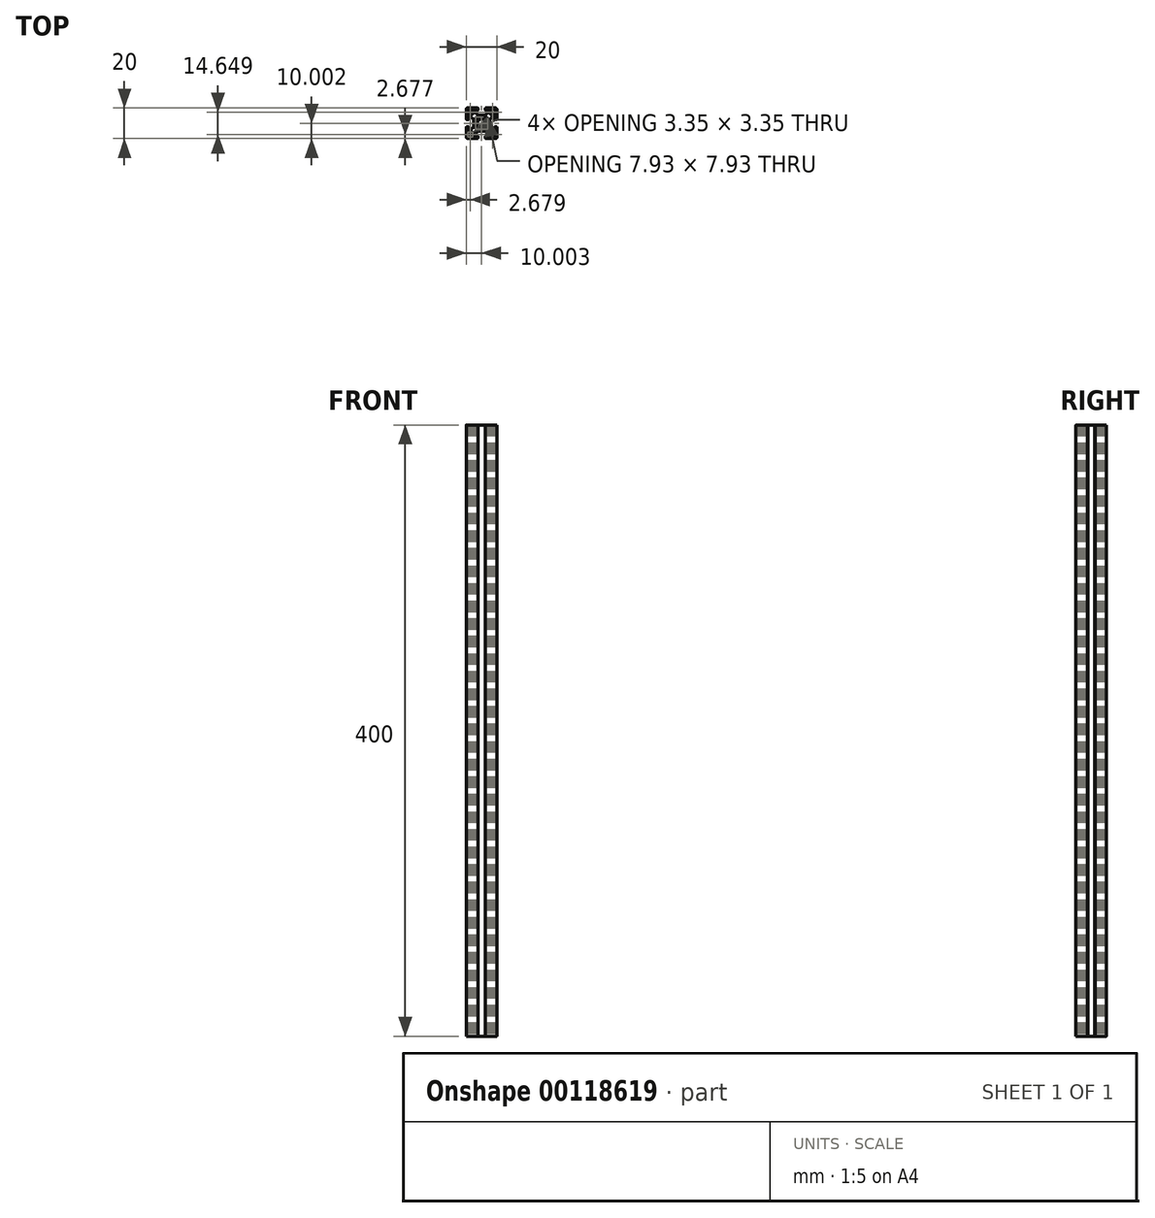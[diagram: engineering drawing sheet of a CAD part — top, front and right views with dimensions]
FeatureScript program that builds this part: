
annotation { "Feature Type Name" : "Feature", "Feature Type Description" : "" }
export const myFeature = defineFeature(function(context is Context, id is Id, definition is map)
    precondition{}
    {
        {
            var Q0;
            Q0=qCreatedBy(makeId("Top.planeOp"),FACE);
            var sketch = newSketch(context, id + "F0", { "sketchPlane" : qUnion([Q0])});
            skLineSegment(sketch, "E0", {"start": v(121.03, 63.35) * mm, "end": v(114.47, 63.35) * mm});
            skLineSegment(sketch, "E1", {"start": v(121.03, 43.35) * mm, "end": v(114.47, 43.35) * mm});
            skLineSegment(sketch, "E2", {"start": v(121.83, 62.55) * mm, "end": v(121.83, 56) * mm});
            skLineSegment(sketch, "E3", {"start": v(101.83, 62.55) * mm, "end": v(101.83, 56) * mm});
            skLineSegment(sketch, "E4", {"start": v(114.18, 58.55) * mm, "end": v(109.48, 58.55) * mm});
            skArc(sketch, "E5", {"start": v(114.47, 63.35) * mm, "mid": v(114.3, 63.28) * mm, "end": v(114.23, 63.11) * mm});
            skLineSegment(sketch, "E6", {"start": v(116.63, 61.75) * mm, "end": v(114.47, 61.75) * mm});
            skArc(sketch, "E7", {"start": v(114.23, 62) * mm, "mid": v(114.3, 61.82) * mm, "end": v(114.47, 61.75) * mm});
            skLineSegment(sketch, "E8", {"start": v(109.2, 61.75) * mm, "end": v(107.03, 61.75) * mm});
            skArc(sketch, "E9", {"start": v(109.2, 61.75) * mm, "mid": v(109.36, 61.82) * mm, "end": v(109.43, 62) * mm});
            skLineSegment(sketch, "E10", {"start": v(107.03, 61) * mm, "end": v(107.03, 61.75) * mm});
            skLineSegment(sketch, "E11", {"start": v(116.63, 61) * mm, "end": v(116.63, 61.75) * mm});
            skLineSegment(sketch, "E12", {"start": v(109.43, 62) * mm, "end": v(109.43, 63.11) * mm});
            skArc(sketch, "E13", {"start": v(109.43, 63.11) * mm, "mid": v(109.36, 63.28) * mm, "end": v(109.2, 63.35) * mm});
            skLineSegment(sketch, "E14", {"start": v(114.23, 62) * mm, "end": v(114.23, 63.11) * mm});
            skLineSegment(sketch, "E15", {"start": v(109.48, 58.55) * mm, "end": v(107.03, 61) * mm});
            skLineSegment(sketch, "E16", {"start": v(114.18, 58.55) * mm, "end": v(116.63, 61) * mm});
            skLineSegment(sketch, "E17", {"start": v(114.18, 48.15) * mm, "end": v(109.48, 48.15) * mm});
            skArc(sketch, "E18", {"start": v(114.23, 43.6) * mm, "mid": v(114.3, 43.42) * mm, "end": v(114.47, 43.35) * mm});
            skLineSegment(sketch, "E19", {"start": v(116.63, 44.95) * mm, "end": v(114.47, 44.95) * mm});
            skArc(sketch, "E20", {"start": v(114.47, 44.95) * mm, "mid": v(114.3, 44.88) * mm, "end": v(114.23, 44.71) * mm});
            skLineSegment(sketch, "E21", {"start": v(109.2, 44.95) * mm, "end": v(107.03, 44.95) * mm});
            skArc(sketch, "E22", {"start": v(109.43, 44.71) * mm, "mid": v(109.36, 44.88) * mm, "end": v(109.2, 44.95) * mm});
            skLineSegment(sketch, "E23", {"start": v(107.03, 45.7) * mm, "end": v(107.03, 44.95) * mm});
            skLineSegment(sketch, "E24", {"start": v(116.63, 45.7) * mm, "end": v(116.63, 44.95) * mm});
            skLineSegment(sketch, "E25", {"start": v(109.43, 44.71) * mm, "end": v(109.43, 43.6) * mm});
            skArc(sketch, "E26", {"start": v(109.2, 43.35) * mm, "mid": v(109.36, 43.42) * mm, "end": v(109.43, 43.6) * mm});
            skLineSegment(sketch, "E27", {"start": v(114.23, 44.71) * mm, "end": v(114.23, 43.6) * mm});
            skLineSegment(sketch, "E28", {"start": v(109.48, 48.15) * mm, "end": v(107.03, 45.7) * mm});
            skLineSegment(sketch, "E29", {"start": v(114.18, 48.15) * mm, "end": v(116.63, 45.7) * mm});
            skLineSegment(sketch, "E30", {"start": v(117.03, 51) * mm, "end": v(117.03, 55.7) * mm});
            skArc(sketch, "E31", {"start": v(121.83, 50.71) * mm, "mid": v(121.76, 50.88) * mm, "end": v(121.6, 50.95) * mm});
            skLineSegment(sketch, "E32", {"start": v(120.23, 48.55) * mm, "end": v(120.23, 50.71) * mm});
            skArc(sketch, "E33", {"start": v(120.47, 50.95) * mm, "mid": v(120.3, 50.88) * mm, "end": v(120.23, 50.71) * mm});
            skLineSegment(sketch, "E34", {"start": v(120.23, 56) * mm, "end": v(120.23, 58.15) * mm});
            skArc(sketch, "E35", {"start": v(120.23, 56) * mm, "mid": v(120.3, 55.82) * mm, "end": v(120.47, 55.75) * mm});
            skLineSegment(sketch, "E36", {"start": v(119.48, 58.15) * mm, "end": v(120.23, 58.15) * mm});
            skLineSegment(sketch, "E37", {"start": v(119.48, 48.55) * mm, "end": v(120.23, 48.55) * mm});
            skLineSegment(sketch, "E38", {"start": v(120.47, 55.75) * mm, "end": v(121.6, 55.75) * mm});
            skArc(sketch, "E39", {"start": v(121.6, 55.75) * mm, "mid": v(121.76, 55.82) * mm, "end": v(121.83, 56) * mm});
            skLineSegment(sketch, "E40", {"start": v(120.47, 50.95) * mm, "end": v(121.6, 50.95) * mm});
            skLineSegment(sketch, "E41", {"start": v(117.03, 55.7) * mm, "end": v(119.48, 58.15) * mm});
            skLineSegment(sketch, "E42", {"start": v(117.03, 51) * mm, "end": v(119.48, 48.55) * mm});
            skArc(sketch, "E43", {"start": v(113.06, 55.78) * mm, "mid": v(111.83, 56.07) * mm, "end": v(110.6, 55.78) * mm});
            skArc(sketch, "E44", {"start": v(109.4, 54.58) * mm, "mid": v(109.11, 53.35) * mm, "end": v(109.4, 52.12) * mm});
            skArc(sketch, "E45", {"start": v(110.6, 50.93) * mm, "mid": v(111.83, 50.63) * mm, "end": v(113.06, 50.93) * mm});
            skArc(sketch, "E46", {"start": v(113.34, 50.88) * mm, "mid": v(113.2, 50.95) * mm, "end": v(113.06, 50.93) * mm});
            skArc(sketch, "E47", {"start": v(113.06, 55.78) * mm, "mid": v(113.2, 55.75) * mm, "end": v(113.34, 55.82) * mm});
            skArc(sketch, "E48", {"start": v(114.26, 52.12) * mm, "mid": v(114.55, 53.35) * mm, "end": v(114.26, 54.58) * mm});
            skArc(sketch, "E49", {"start": v(114.26, 52.12) * mm, "mid": v(114.24, 51.98) * mm, "end": v(114.3, 51.84) * mm});
            skArc(sketch, "E50", {"start": v(114.3, 54.86) * mm, "mid": v(114.24, 54.73) * mm, "end": v(114.26, 54.58) * mm});
            skLineSegment(sketch, "E51", {"start": v(114.3, 54.86) * mm, "end": v(114.7, 55.26) * mm});
            skLineSegment(sketch, "E52", {"start": v(113.34, 55.82) * mm, "end": v(113.74, 56.22) * mm});
            skLineSegment(sketch, "E53", {"start": v(113.34, 50.88) * mm, "end": v(113.74, 50.49) * mm});
            skLineSegment(sketch, "E54", {"start": v(114.3, 51.84) * mm, "end": v(114.7, 51.45) * mm});
            skArc(sketch, "E55", {"start": v(114.7, 55.26) * mm, "mid": v(115.51, 57.03) * mm, "end": v(113.74, 56.22) * mm});
            skArc(sketch, "E56", {"start": v(113.74, 50.49) * mm, "mid": v(115.51, 49.67) * mm, "end": v(114.7, 51.45) * mm});
            skArc(sketch, "E57", {"start": v(110.6, 50.93) * mm, "mid": v(110.46, 50.95) * mm, "end": v(110.32, 50.88) * mm});
            skArc(sketch, "E58", {"start": v(110.32, 55.82) * mm, "mid": v(110.46, 55.75) * mm, "end": v(110.6, 55.78) * mm});
            skArc(sketch, "E59", {"start": v(109.36, 51.84) * mm, "mid": v(109.43, 51.98) * mm, "end": v(109.4, 52.12) * mm});
            skArc(sketch, "E60", {"start": v(109.4, 54.58) * mm, "mid": v(109.43, 54.73) * mm, "end": v(109.36, 54.86) * mm});
            skLineSegment(sketch, "E61", {"start": v(109.36, 54.86) * mm, "end": v(108.97, 55.26) * mm});
            skLineSegment(sketch, "E62", {"start": v(110.32, 50.88) * mm, "end": v(109.93, 50.49) * mm});
            skLineSegment(sketch, "E63", {"start": v(109.36, 51.84) * mm, "end": v(108.97, 51.45) * mm});
            skArc(sketch, "E64", {"start": v(109.93, 56.22) * mm, "mid": v(108.16, 57.03) * mm, "end": v(108.97, 55.26) * mm});
            skArc(sketch, "E65", {"start": v(108.97, 51.45) * mm, "mid": v(108.16, 49.67) * mm, "end": v(109.93, 50.49) * mm});
            skLineSegment(sketch, "E66", {"start": v(110.32, 55.82) * mm, "end": v(109.93, 56.22) * mm});
            skLineSegment(sketch, "E67", {"start": v(117.82, 61.4) * mm, "end": v(118.28, 60.93) * mm});
            skLineSegment(sketch, "E68", {"start": v(119.41, 59.8) * mm, "end": v(119.88, 59.34) * mm});
            skLineSegment(sketch, "E69", {"start": v(120.83, 61.15) * mm, "end": v(120.83, 59.73) * mm});
            skLineSegment(sketch, "E70", {"start": v(119.63, 62.35) * mm, "end": v(118.21, 62.35) * mm});
            skArc(sketch, "E71", {"start": v(120.83, 61.15) * mm, "mid": v(120.48, 62) * mm, "end": v(119.63, 62.35) * mm});
            skLineSegment(sketch, "E72", {"start": v(118.28, 60.93) * mm, "end": v(117.72, 60.37) * mm});
            skLineSegment(sketch, "E73", {"start": v(119.41, 59.8) * mm, "end": v(118.85, 59.23) * mm});
            skArc(sketch, "E74", {"start": v(117.72, 60.37) * mm, "mid": v(117.72, 59.23) * mm, "end": v(118.85, 59.23) * mm});
            skArc(sketch, "E75", {"start": v(119.88, 59.34) * mm, "mid": v(120.49, 59.22) * mm, "end": v(120.83, 59.73) * mm});
            skArc(sketch, "E76", {"start": v(118.21, 62.35) * mm, "mid": v(117.7, 62) * mm, "end": v(117.82, 61.4) * mm});
            skLineSegment(sketch, "E77", {"start": v(117.82, 45.3) * mm, "end": v(118.28, 45.77) * mm});
            skLineSegment(sketch, "E78", {"start": v(119.41, 46.9) * mm, "end": v(119.88, 47.37) * mm});
            skLineSegment(sketch, "E79", {"start": v(120.83, 45.55) * mm, "end": v(120.83, 46.97) * mm});
            skLineSegment(sketch, "E80", {"start": v(119.63, 44.35) * mm, "end": v(118.21, 44.35) * mm});
            skArc(sketch, "E81", {"start": v(119.63, 44.35) * mm, "mid": v(120.48, 44.7) * mm, "end": v(120.83, 45.55) * mm});
            skLineSegment(sketch, "E82", {"start": v(118.28, 45.77) * mm, "end": v(117.72, 46.34) * mm});
            skLineSegment(sketch, "E83", {"start": v(119.41, 46.9) * mm, "end": v(118.85, 47.47) * mm});
            skArc(sketch, "E84", {"start": v(118.85, 47.47) * mm, "mid": v(117.72, 47.47) * mm, "end": v(117.72, 46.34) * mm});
            skArc(sketch, "E85", {"start": v(120.83, 46.97) * mm, "mid": v(120.49, 47.49) * mm, "end": v(119.88, 47.37) * mm});
            skArc(sketch, "E86", {"start": v(117.82, 45.3) * mm, "mid": v(117.7, 44.7) * mm, "end": v(118.21, 44.35) * mm});
            skLineSegment(sketch, "E87", {"start": v(106.63, 51) * mm, "end": v(106.63, 55.7) * mm});
            skArc(sketch, "E88", {"start": v(102.07, 50.95) * mm, "mid": v(101.9, 50.88) * mm, "end": v(101.83, 50.71) * mm});
            skLineSegment(sketch, "E89", {"start": v(103.43, 48.55) * mm, "end": v(103.43, 50.71) * mm});
            skArc(sketch, "E90", {"start": v(103.43, 50.71) * mm, "mid": v(103.36, 50.88) * mm, "end": v(103.2, 50.95) * mm});
            skLineSegment(sketch, "E91", {"start": v(103.43, 56) * mm, "end": v(103.43, 58.15) * mm});
            skArc(sketch, "E92", {"start": v(103.2, 55.75) * mm, "mid": v(103.36, 55.82) * mm, "end": v(103.43, 56) * mm});
            skLineSegment(sketch, "E93", {"start": v(104.18, 58.15) * mm, "end": v(103.43, 58.15) * mm});
            skLineSegment(sketch, "E94", {"start": v(104.18, 48.55) * mm, "end": v(103.43, 48.55) * mm});
            skLineSegment(sketch, "E95", {"start": v(103.2, 55.75) * mm, "end": v(102.07, 55.75) * mm});
            skArc(sketch, "E96", {"start": v(101.83, 56) * mm, "mid": v(101.9, 55.82) * mm, "end": v(102.07, 55.75) * mm});
            skLineSegment(sketch, "E97", {"start": v(103.2, 50.95) * mm, "end": v(102.07, 50.95) * mm});
            skLineSegment(sketch, "E98", {"start": v(106.63, 55.7) * mm, "end": v(104.18, 58.15) * mm});
            skLineSegment(sketch, "E99", {"start": v(106.63, 51) * mm, "end": v(104.18, 48.55) * mm});
            skLineSegment(sketch, "E100", {"start": v(121.83, 50.71) * mm, "end": v(121.83, 44.15) * mm});
            skLineSegment(sketch, "E101", {"start": v(109.2, 63.35) * mm, "end": v(102.63, 63.35) * mm});
            skLineSegment(sketch, "E102", {"start": v(101.83, 50.71) * mm, "end": v(101.83, 44.15) * mm});
            skLineSegment(sketch, "E103", {"start": v(109.2, 43.35) * mm, "end": v(102.63, 43.35) * mm});
            skLineSegment(sketch, "E104", {"start": v(105.85, 61.4) * mm, "end": v(105.38, 60.93) * mm});
            skLineSegment(sketch, "E105", {"start": v(104.25, 59.8) * mm, "end": v(103.79, 59.34) * mm});
            skLineSegment(sketch, "E106", {"start": v(102.83, 61.15) * mm, "end": v(102.83, 59.73) * mm});
            skLineSegment(sketch, "E107", {"start": v(104.03, 62.35) * mm, "end": v(105.45, 62.35) * mm});
            skArc(sketch, "E108", {"start": v(104.03, 62.35) * mm, "mid": v(103.18, 62) * mm, "end": v(102.83, 61.15) * mm});
            skLineSegment(sketch, "E109", {"start": v(105.38, 60.93) * mm, "end": v(105.95, 60.37) * mm});
            skLineSegment(sketch, "E110", {"start": v(104.25, 59.8) * mm, "end": v(104.82, 59.23) * mm});
            skArc(sketch, "E111", {"start": v(104.82, 59.23) * mm, "mid": v(105.95, 59.23) * mm, "end": v(105.95, 60.37) * mm});
            skArc(sketch, "E112", {"start": v(102.83, 59.73) * mm, "mid": v(103.18, 59.22) * mm, "end": v(103.79, 59.34) * mm});
            skArc(sketch, "E113", {"start": v(105.85, 61.4) * mm, "mid": v(105.97, 62) * mm, "end": v(105.45, 62.35) * mm});
            skLineSegment(sketch, "E114", {"start": v(105.85, 45.3) * mm, "end": v(105.38, 45.77) * mm});
            skLineSegment(sketch, "E115", {"start": v(104.25, 46.9) * mm, "end": v(103.79, 47.37) * mm});
            skLineSegment(sketch, "E116", {"start": v(102.83, 45.55) * mm, "end": v(102.83, 46.97) * mm});
            skLineSegment(sketch, "E117", {"start": v(104.03, 44.35) * mm, "end": v(105.45, 44.35) * mm});
            skArc(sketch, "E118", {"start": v(102.83, 45.55) * mm, "mid": v(103.18, 44.7) * mm, "end": v(104.03, 44.35) * mm});
            skLineSegment(sketch, "E119", {"start": v(105.38, 45.77) * mm, "end": v(105.95, 46.34) * mm});
            skLineSegment(sketch, "E120", {"start": v(104.25, 46.9) * mm, "end": v(104.82, 47.47) * mm});
            skArc(sketch, "E121", {"start": v(105.95, 46.34) * mm, "mid": v(105.95, 47.47) * mm, "end": v(104.82, 47.47) * mm});
            skArc(sketch, "E122", {"start": v(103.79, 47.37) * mm, "mid": v(103.18, 47.49) * mm, "end": v(102.83, 46.97) * mm});
            skArc(sketch, "E123", {"start": v(105.45, 44.35) * mm, "mid": v(105.97, 44.7) * mm, "end": v(105.85, 45.3) * mm});
            skArc(sketch, "E124", {"start": v(121.83, 62.55) * mm, "mid": v(121.6, 63.12) * mm, "end": v(121.03, 63.35) * mm});
            skArc(sketch, "E125", {"start": v(121.03, 43.35) * mm, "mid": v(121.6, 43.59) * mm, "end": v(121.83, 44.15) * mm});
            skArc(sketch, "E126", {"start": v(101.83, 44.15) * mm, "mid": v(102.07, 43.59) * mm, "end": v(102.63, 43.35) * mm});
            skArc(sketch, "E127", {"start": v(102.63, 63.35) * mm, "mid": v(102.07, 63.12) * mm, "end": v(101.83, 62.55) * mm});
            skCircle(sketch, "E128", {"center": v(111.83, 53.35) * mm, "radius": 2.72 * mm});
            skSolve(sketch);
        }
        {
            var Q0;
            Q0=makeQuery(id+"F0.imprint","IMPRINT",FACE,{"disambiguationData":[TD([[makeQuery(id+"F0.imprint","IMPRINT",EDGE,{"derivedFrom":sQuery(id+"F0.wireOp",EDGE,"E0")}),1.0]])]});
            extrude(context, id + "F1", {"entities" : qUnion([Q0]), "depth" : 400 * mm});
        }
        {
            var Q0;
            Q0=makeQuery(id+"F1.opExtrude","SWEPT_FACE",FACE,{"disambiguationData":[OSD([sQuery(id+"F0.wireOp",EDGE,"E0")])]});
            var sketch = newSketch(context, id + "F2", { "sketchPlane" : qUnion([Q0])});
            skLineSegment(sketch, "E129.0", {"start": v(-121.83, 400) * mm, "end": v(-121.83, 0) * mm, "construction": true});
            skLineSegment(sketch, "E129.1", {"start": v(-101.83, 400) * mm, "end": v(-101.83, 0) * mm, "construction": true});
            skLineSegment(sketch, "E130", {"start": v(-101.83, 400) * mm, "end": v(-121.83, 400) * mm, "construction": true});
            skLineSegment(sketch, "E131", {"start": v(-121.83, 390) * mm, "end": v(-101.83, 390) * mm, "construction": true});
            skLineSegment(sketch, "E132", {"start": v(-121.83, 10) * mm, "end": v(-101.83, 10) * mm, "construction": true});
            skLineSegment(sketch, "E133", {"start": v(-121.83, 0) * mm, "end": v(-101.83, 0) * mm, "construction": true});
            skLineSegment(sketch, "E134", {"start": v(-101.83, 200) * mm, "end": v(-121.83, 200) * mm, "construction": true});
            skSolve(sketch);
        }
        {
            var Q0;
            Q0=makeQuery(id+"F1.opExtrude","SWEPT_FACE",FACE,{"disambiguationData":[OSD([sQuery(id+"F0.wireOp",EDGE,"E3")])]});
            var sketch = newSketch(context, id + "F3", { "sketchPlane" : qUnion([Q0])});
            skLineSegment(sketch, "E135.0", {"start": v(-63.35, 400) * mm, "end": v(-63.35, 0) * mm, "construction": true});
            skLineSegment(sketch, "E136.0", {"start": v(-43.35, 400) * mm, "end": v(-43.35, 0) * mm, "construction": true});
            skLineSegment(sketch, "E137", {"start": v(-63.35, 390) * mm, "end": v(-43.35, 390) * mm, "construction": true});
            skLineSegment(sketch, "E138", {"start": v(-63.35, 10) * mm, "end": v(-43.35, 10) * mm, "construction": true});
            skLineSegment(sketch, "E139", {"start": v(-63.35, 200) * mm, "end": v(-43.35, 200) * mm, "construction": true});
            skSolve(sketch);
        }
        {
            var Q0;
            Q0=makeQuery(id+"F1.opExtrude","SWEPT_FACE",FACE,{"disambiguationData":[OSD([sQuery(id+"F0.wireOp",EDGE,"E103")])]});
            var sketch = newSketch(context, id + "F4", { "sketchPlane" : qUnion([Q0])});
            skLineSegment(sketch, "E140.0", {"start": v(101.83, 400) * mm, "end": v(101.83, 0) * mm, "construction": true});
            skLineSegment(sketch, "E140.1", {"start": v(121.83, 400) * mm, "end": v(121.83, 0) * mm, "construction": true});
            skLineSegment(sketch, "E141", {"start": v(121.83, 390) * mm, "end": v(101.83, 390) * mm, "construction": true});
            skLineSegment(sketch, "E142", {"start": v(121.83, 10) * mm, "end": v(101.83, 10) * mm, "construction": true});
            skLineSegment(sketch, "E143", {"start": v(121.83, 200) * mm, "end": v(101.83, 200) * mm, "construction": true});
            skSolve(sketch);
        }
        {
            var Q0;
            Q0=makeQuery(id+"F1.opExtrude","SWEPT_FACE",FACE,{"disambiguationData":[OSD([sQuery(id+"F0.wireOp",EDGE,"E2")])]});
            var sketch = newSketch(context, id + "F5", { "sketchPlane" : qUnion([Q0])});
            skLineSegment(sketch, "E144.0", {"start": v(63.35, 400) * mm, "end": v(63.35, 0) * mm, "construction": true});
            skLineSegment(sketch, "E144.1", {"start": v(43.35, 400) * mm, "end": v(43.35, 0) * mm, "construction": true});
            skLineSegment(sketch, "E145", {"start": v(63.35, 10) * mm, "end": v(43.35, 10) * mm, "construction": true});
            skLineSegment(sketch, "E146", {"start": v(63.35, 390) * mm, "end": v(43.35, 390) * mm, "construction": true});
            skLineSegment(sketch, "E147", {"start": v(63.35, 200) * mm, "end": v(43.35, 200) * mm, "construction": true});
            skSolve(sketch);
        }
    });
